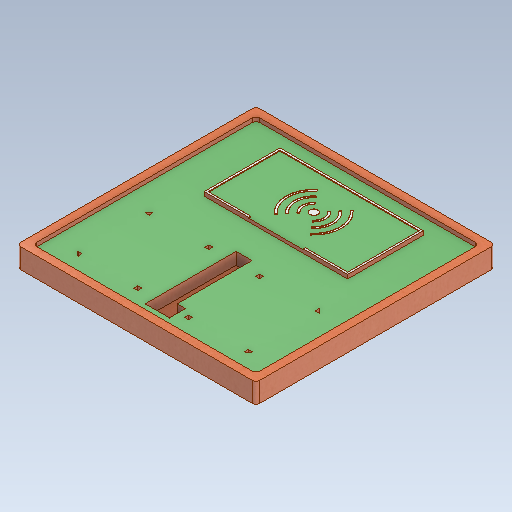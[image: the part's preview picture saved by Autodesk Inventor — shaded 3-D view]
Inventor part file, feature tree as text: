
AUTODESK INVENTOR PART (.ipt)
format: ipt  version: 2021 (Build 250183000, 183)  size: 363,520 bytes
history: native  units: mm
features: extrude x9, sketch x8, fillet x2, chamfer x2
ambient origin geometry x8: Origin, YZ Plane, XZ Plane, XY Plane, X Axis, Y Axis, Z Axis, Center Point
bodies: Solid1 (feature_tree)
feature tree (21):
  extrude  "Extrusion1"  Depth=300.0mm
  extrude  "Extrusion2"  Depth=10.0mm
  fillet  "Fillet1"  Radius=10.0mm
  fillet  "Fillet2"  Radius=10.0mm
  extrude  "Extrusion3"  Depth=5.0mm TaperAngle=0.0deg
  extrude  "Extrusion4"  Depth=5.0mm
  extrude  "Extrusion6"  Depth=20.0mm
  extrude  "Extrusion9"  Depth=50.0mm
  extrude  "Extrusion11"  Depth=2.5mm
  extrude  "Extrusion12"  Depth=2.5mm
  extrude  "Extrusion13"  Depth=2.5mm
  chamfer  "Chamfer1"  Distance=1.0mm
  chamfer  "Chamfer2"  Distance=70.0mm
  sketch  "Sketch1"  dims[d0=300.0mm d1=300.0mm]
  sketch  "Sketch2"  dims[d2=25.0mm d3=0.0mm d4=10.0mm d5=10.0mm d6=10.0mm]
  sketch  "Sketch3"  dims[d7=10.0mm d8=5.0mm d9=0.0mm]
  sketch  "Sketch5"  dims[d10=5.0mm d11=5.0mm]
  sketch  "Sketch8"  dims[d12=95.0mm d13=20.0mm]
  sketch  "Sketch11"  dims[d14=50.0mm d15=50.0mm]
  sketch  "Sketch12"  dims[d16=5.0mm d17=0.0mm d18=2.5mm]
  sketch  "Sketch13"  dims[d19=2.5mm d20=2.5mm d21=2.5mm d22=1.0mm d23=0.0mm d47=70.0mm d48=65.0mm d49=50.0mm d50=45.0mm d51=30.0mm d52=25.0mm d53=10.0mm d55=0.5mm d56=0.0mm d64=69.0mm d72=34.25mm d74=34.25mm d75=1.0mm d76=0.0mm d85=6.0mm d86=0.0mm d87=50.0mm d90=94.0mm d91=5.0mm d92=5.0mm d93=5.0mm d97=15.0mm d98=0.0mm d100=10.0mm d101=10.0mm d105=70.0mm d106=5.0mm d107=5.0mm d108=5.0mm d109=5.0mm d110=70.0mm d111=5.0mm d112=70.0mm d113=5.0mm d114=15.0mm d115=0.0mm d116=4.0mm d117=2.0mm d118=45.0deg d119=4.0mm d120=2.0mm d121=45.0deg]
